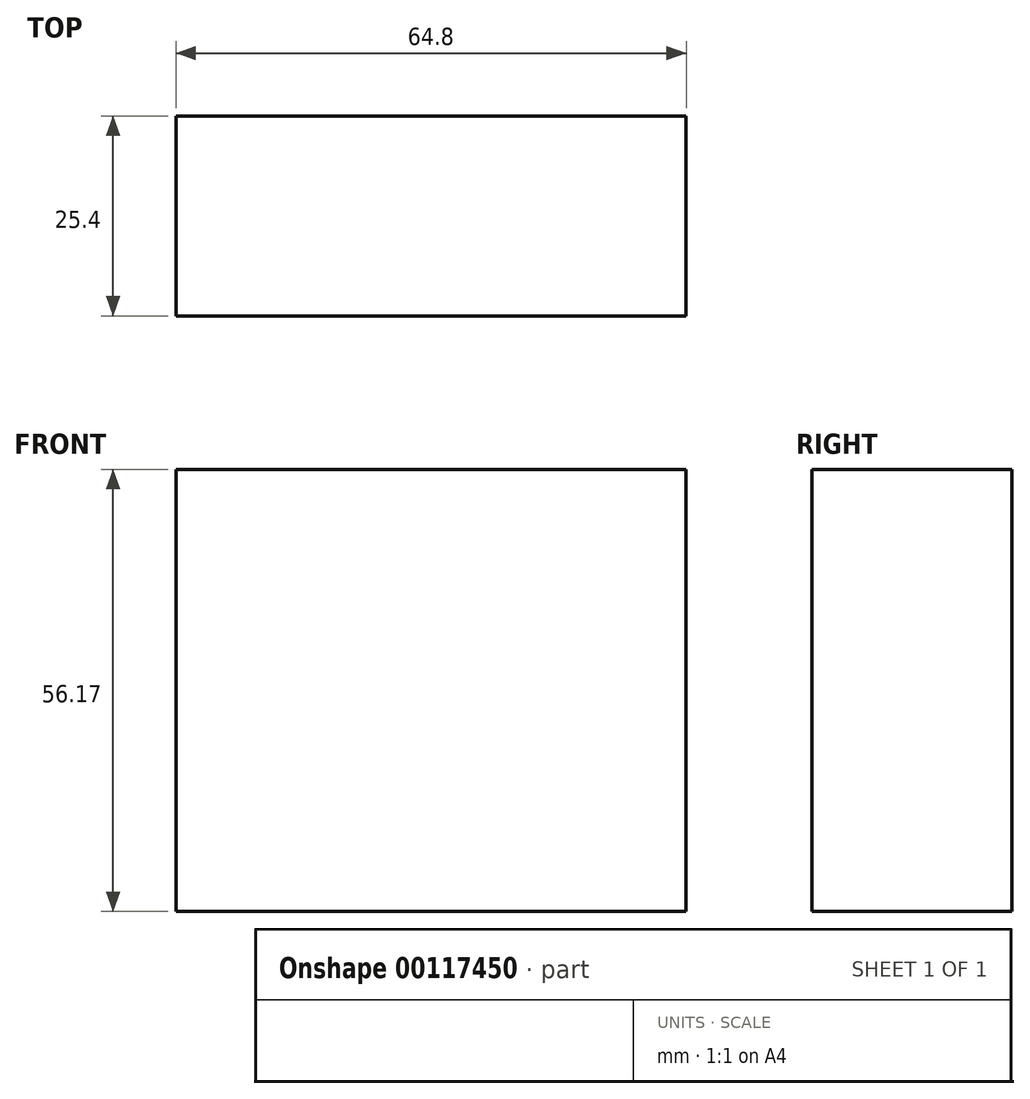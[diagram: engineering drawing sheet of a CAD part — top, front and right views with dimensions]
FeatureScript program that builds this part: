
annotation { "Feature Type Name" : "Feature", "Feature Type Description" : "" }
export const myFeature = defineFeature(function(context is Context, id is Id, definition is map)
    precondition{}
    {
        {
            var Q0;
            Q0=qCreatedBy(makeId("Front.planeOp"),FACE);
            var sketch = newSketch(context, id + "F0", { "sketchPlane" : qUnion([Q0])});
            skLineSegment(sketch, "E0", {"start": v(0, 0) * mm, "end": v(64.8, 0) * mm});
            skLineSegment(sketch, "E1", {"start": v(64.8, 0) * mm, "end": v(64.8, 56.17) * mm});
            skLineSegment(sketch, "E2", {"start": v(64.8, 56.17) * mm, "end": v(0, 56.17) * mm});
            skLineSegment(sketch, "E3", {"start": v(0, 56.17) * mm, "end": v(0, 0) * mm});
            skSolve(sketch);
        }
        {
            var Q0;
            Q0 = qSketchRegion(id + "F0", true);
            extrude(context, id + "F1", {"entities" : qUnion([Q0]), "depth" : 25.4 * mm});
        }
    });
